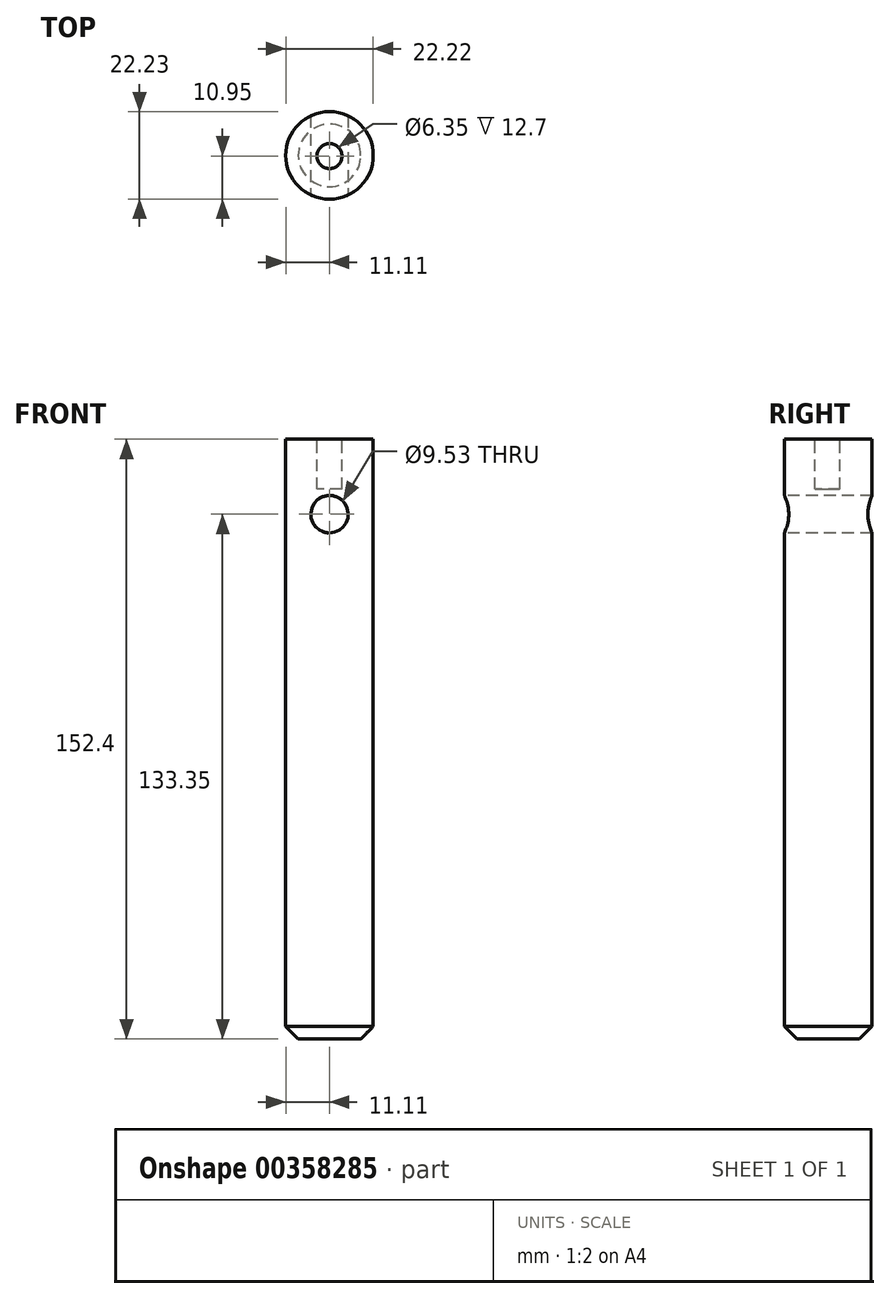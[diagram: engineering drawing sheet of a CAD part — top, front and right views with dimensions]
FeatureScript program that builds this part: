
annotation { "Feature Type Name" : "Feature", "Feature Type Description" : "" }
export const myFeature = defineFeature(function(context is Context, id is Id, definition is map)
    precondition{}
    {
        {
            var Q0;
            Q0=qCreatedBy(makeId("Top.planeOp"),FACE);
            var sketch = newSketch(context, id + "F0", { "sketchPlane" : qUnion([Q0])});
            skCircle(sketch, "E0", {"center": v(0, 0.17) * mm, "radius": 11.11 * mm});
            skSolve(sketch);
        }
        {
            var Q0;
            Q0=qSketchRegion(id+"F0",true);
            extrude(context, id + "F1", {"entities" : qUnion([Q0]), "depth" : 152.4 * mm});
        }
        {
            var Q0;
            Q0=makeQuery(id+"F1.opExtrude","CAP_EDGE",EDGE,{"disambiguationData":[OSD([sQuery(id+"F0.wireOp",EDGE,"E0")])],"isStart":true});
            chamfer(context, id + "F2", {"entities" : qUnion([Q0]), "width" : 3.17 * mm, "tangentPropagation" : true});
        }
        {
            var Q0;
            Q0=qCreatedBy(makeId("Front.planeOp"),FACE);
            var sketch = newSketch(context, id + "F3", { "sketchPlane" : qUnion([Q0])});
            skCircle(sketch, "E1", {"center": v(0, 133.35) * mm, "radius": 4.76 * mm});
            skSolve(sketch);
        }
        {
            var Q0;
            Q0=qSketchRegion(id+"F3",true);
            extrude(context, id + "F4", {"entities" : qUnion([Q0]), "operationType" : NewBodyOperationType.REMOVE, "oppositeDirection" : true, "depth" : 25.4 * mm, "hasSecondDirection" : true, "secondDirectionOppositeDirection" : false, "secondDirectionDepth" : 25.4 * mm});
        }
        {
            var Q0;
            Q0=makeQuery(id+"F1.opExtrude","CAP_FACE",FACE,{"disambiguationData":[OSD([sQuery(id+"F0.wireOp",EDGE,"E0")])],"isStart":false});
            var sketch = newSketch(context, id + "F5", { "sketchPlane" : qUnion([Q0])});
            skCircle(sketch, "E2", {"center": v(0, 0) * mm, "radius": 3.18 * mm});
            skSolve(sketch);
        }
        {
            var Q0;
            Q0=qSketchRegion(id+"F5",true);
            extrude(context, id + "F6", {"entities" : qUnion([Q0]), "operationType" : NewBodyOperationType.REMOVE, "oppositeDirection" : true, "depth" : 12.7 * mm});
        }
    });
